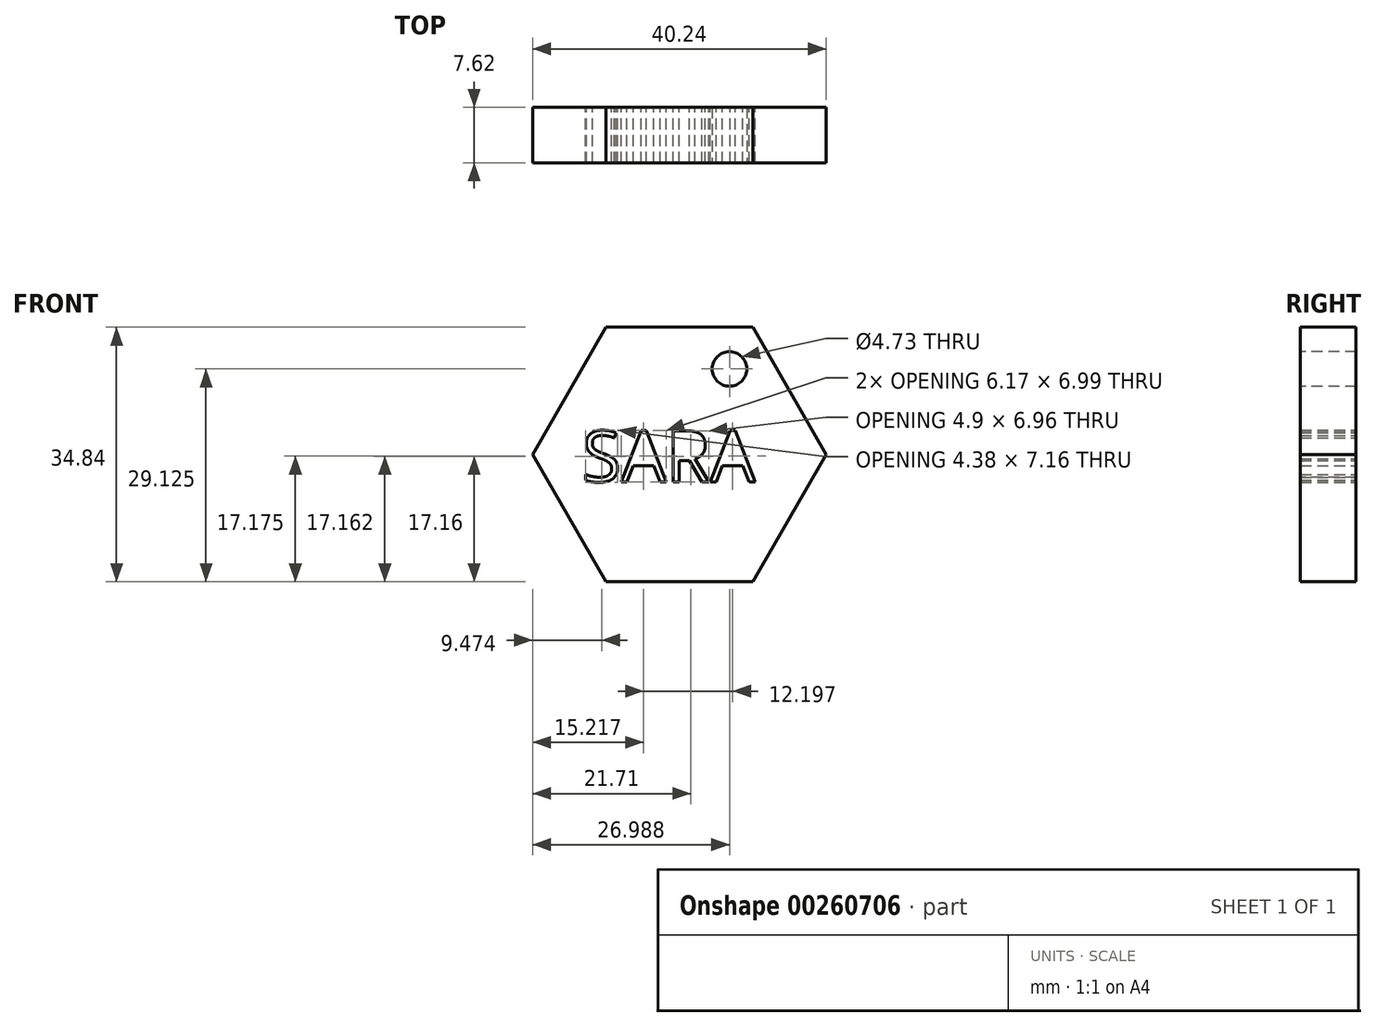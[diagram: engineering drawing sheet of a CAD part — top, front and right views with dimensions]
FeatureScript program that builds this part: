
annotation { "Feature Type Name" : "Feature", "Feature Type Description" : "" }
export const myFeature = defineFeature(function(context is Context, id is Id, definition is map)
    precondition{}
    {
        {
            var Q0;
            Q0=qCreatedBy(makeId("Front.planeOp"),FACE);
            var sketch = newSketch(context, id + "F0", { "sketchPlane" : qUnion([Q0])});
            skCircle(sketch, "E0.cCircle", {"center": v(0, 0) * mm, "radius": 17.42 * mm, "construction": true});
            skLineSegment(sketch, "E0.0", {"start": v(-10.06, 17.42) * mm, "end": v(10.06, 17.42) * mm});
            skLineSegment(sketch, "E0.1", {"start": v(10.06, 17.42) * mm, "end": v(20.12, 0) * mm});
            skLineSegment(sketch, "E0.2", {"start": v(20.12, 0) * mm, "end": v(10.06, -17.42) * mm});
            skLineSegment(sketch, "E0.3", {"start": v(10.06, -17.42) * mm, "end": v(-10.06, -17.42) * mm});
            skLineSegment(sketch, "E0.4", {"start": v(-10.06, -17.42) * mm, "end": v(-20.12, 0) * mm});
            skLineSegment(sketch, "E0.5", {"start": v(-20.12, 0) * mm, "end": v(-10.06, 17.42) * mm});
            skPoint(sketch, "E0.0.midPoint", {"position": v(0, 17.42) * mm});
            skPoint(sketch, "E1.secondSnap0", {"position": v(15.09, 8.71) * mm});
            skText(sketch, "E2", { "text": "SARA", "fontName": "OpenSans-Regular.ttf"});
            const initialGuessF0  = {"E2": [-0.01334, -0.00374, 1, 0, 0.00702]};
            skSetInitialGuess(sketch, initialGuessF0);
            skSolve(sketch);
        }
        {
            var Q0;
            Q0=makeQuery(id+"F0.imprint","IMPRINT",FACE,{"disambiguationData":[TD([[makeQuery(id+"F0.imprint","IMPRINT",EDGE,{"derivedFrom":sQuery(id+"F0.wireOp",EDGE,"E0.0")}),-1.0]])]});
            extrude(context, id + "F1", {"entities" : qUnion([Q0]), "depth" : 7.62 * mm});
        }
        {
            var Q0;
            Q0=makeQuery(id+"F1.opExtrude","CAP_FACE",FACE,{"disambiguationData":[OSD([sQuery(id+"F0.wireOp",EDGE,"E0.0"),sQuery(id+"F0.wireOp",EDGE,"E0.1"),sQuery(id+"F0.wireOp",EDGE,"E0.2"),sQuery(id+"F0.wireOp",EDGE,"E0.3"),sQuery(id+"F0.wireOp",EDGE,"E0.4"),sQuery(id+"F0.wireOp",EDGE,"E0.5"),sQuery(id+"F0.wireOp",EDGE,"E2.sketch_text.stroke-0"),sQuery(id+"F0.wireOp",EDGE,"E2.sketch_text.stroke-1"),sQuery(id+"F0.wireOp",EDGE,"E2.sketch_text.stroke-2"),sQuery(id+"F0.wireOp",EDGE,"E2.sketch_text.stroke-3"),sQuery(id+"F0.wireOp",EDGE,"E2.sketch_text.stroke-4"),sQuery(id+"F0.wireOp",EDGE,"E2.sketch_text.stroke-5"),sQuery(id+"F0.wireOp",EDGE,"E2.sketch_text.stroke-6"),sQuery(id+"F0.wireOp",EDGE,"E2.sketch_text.stroke-7"),sQuery(id+"F0.wireOp",EDGE,"E2.sketch_text.stroke-8"),sQuery(id+"F0.wireOp",EDGE,"E2.sketch_text.stroke-9"),sQuery(id+"F0.wireOp",EDGE,"E2.sketch_text.stroke-10"),sQuery(id+"F0.wireOp",EDGE,"E2.sketch_text.stroke-11"),sQuery(id+"F0.wireOp",EDGE,"E2.sketch_text.stroke-12"),sQuery(id+"F0.wireOp",EDGE,"E2.sketch_text.stroke-13"),sQuery(id+"F0.wireOp",EDGE,"E2.sketch_text.stroke-14"),sQuery(id+"F0.wireOp",EDGE,"E2.sketch_text.stroke-15"),sQuery(id+"F0.wireOp",EDGE,"E2.sketch_text.stroke-16"),sQuery(id+"F0.wireOp",EDGE,"E2.sketch_text.stroke-17"),sQuery(id+"F0.wireOp",EDGE,"E2.sketch_text.stroke-18"),sQuery(id+"F0.wireOp",EDGE,"E2.sketch_text.stroke-19"),sQuery(id+"F0.wireOp",EDGE,"E2.sketch_text.stroke-20"),sQuery(id+"F0.wireOp",EDGE,"E2.sketch_text.stroke-21"),sQuery(id+"F0.wireOp",EDGE,"E2.sketch_text.stroke-22"),sQuery(id+"F0.wireOp",EDGE,"E2.sketch_text.stroke-23"),sQuery(id+"F0.wireOp",EDGE,"E2.sketch_text.stroke-24"),sQuery(id+"F0.wireOp",EDGE,"E2.sketch_text.stroke-25"),sQuery(id+"F0.wireOp",EDGE,"E2.sketch_text.stroke-26"),sQuery(id+"F0.wireOp",EDGE,"E2.sketch_text.stroke-27"),sQuery(id+"F0.wireOp",EDGE,"E2.sketch_text.stroke-28"),sQuery(id+"F0.wireOp",EDGE,"E2.sketch_text.stroke-29"),sQuery(id+"F0.wireOp",EDGE,"E2.sketch_text.stroke-30"),sQuery(id+"F0.wireOp",EDGE,"E2.sketch_text.stroke-31"),sQuery(id+"F0.wireOp",EDGE,"E2.sketch_text.stroke-32"),sQuery(id+"F0.wireOp",EDGE,"E2.sketch_text.stroke-38"),sQuery(id+"F0.wireOp",EDGE,"E2.sketch_text.stroke-39"),sQuery(id+"F0.wireOp",EDGE,"E2.sketch_text.stroke-40"),sQuery(id+"F0.wireOp",EDGE,"E2.sketch_text.stroke-41"),sQuery(id+"F0.wireOp",EDGE,"E2.sketch_text.stroke-42"),sQuery(id+"F0.wireOp",EDGE,"E2.sketch_text.stroke-43"),sQuery(id+"F0.wireOp",EDGE,"E2.sketch_text.stroke-44"),sQuery(id+"F0.wireOp",EDGE,"E2.sketch_text.stroke-45"),sQuery(id+"F0.wireOp",EDGE,"E2.sketch_text.stroke-46"),sQuery(id+"F0.wireOp",EDGE,"E2.sketch_text.stroke-47"),sQuery(id+"F0.wireOp",EDGE,"E2.sketch_text.stroke-48"),sQuery(id+"F0.wireOp",EDGE,"E2.sketch_text.stroke-56"),sQuery(id+"F0.wireOp",EDGE,"E2.sketch_text.stroke-57"),sQuery(id+"F0.wireOp",EDGE,"E2.sketch_text.stroke-58"),sQuery(id+"F0.wireOp",EDGE,"E2.sketch_text.stroke-59"),sQuery(id+"F0.wireOp",EDGE,"E2.sketch_text.stroke-60"),sQuery(id+"F0.wireOp",EDGE,"E2.sketch_text.stroke-61"),sQuery(id+"F0.wireOp",EDGE,"E2.sketch_text.stroke-62"),sQuery(id+"F0.wireOp",EDGE,"E2.sketch_text.stroke-63")])],"isStart":false});
            var sketch = newSketch(context, id + "F2", { "sketchPlane" : qUnion([Q0])});
            skCircle(sketch, "E3", {"center": v(6.87, 11.7) * mm, "radius": 2.37 * mm});
            skSolve(sketch);
        }
        {
            var Q0;
            Q0=makeQuery(id+"F2.imprint","IMPRINT",FACE,{"disambiguationData":[TD([[makeQuery(id+"F2.imprint","IMPRINT",EDGE,{"derivedFrom":sQuery(id+"F2.wireOp",EDGE,"E3")}),1.0]])]});
            extrude(context, id + "F3", {"entities" : qUnion([Q0]), "operationType" : NewBodyOperationType.REMOVE, "oppositeDirection" : true, "depth" : 25.4 * mm});
        }
    });
